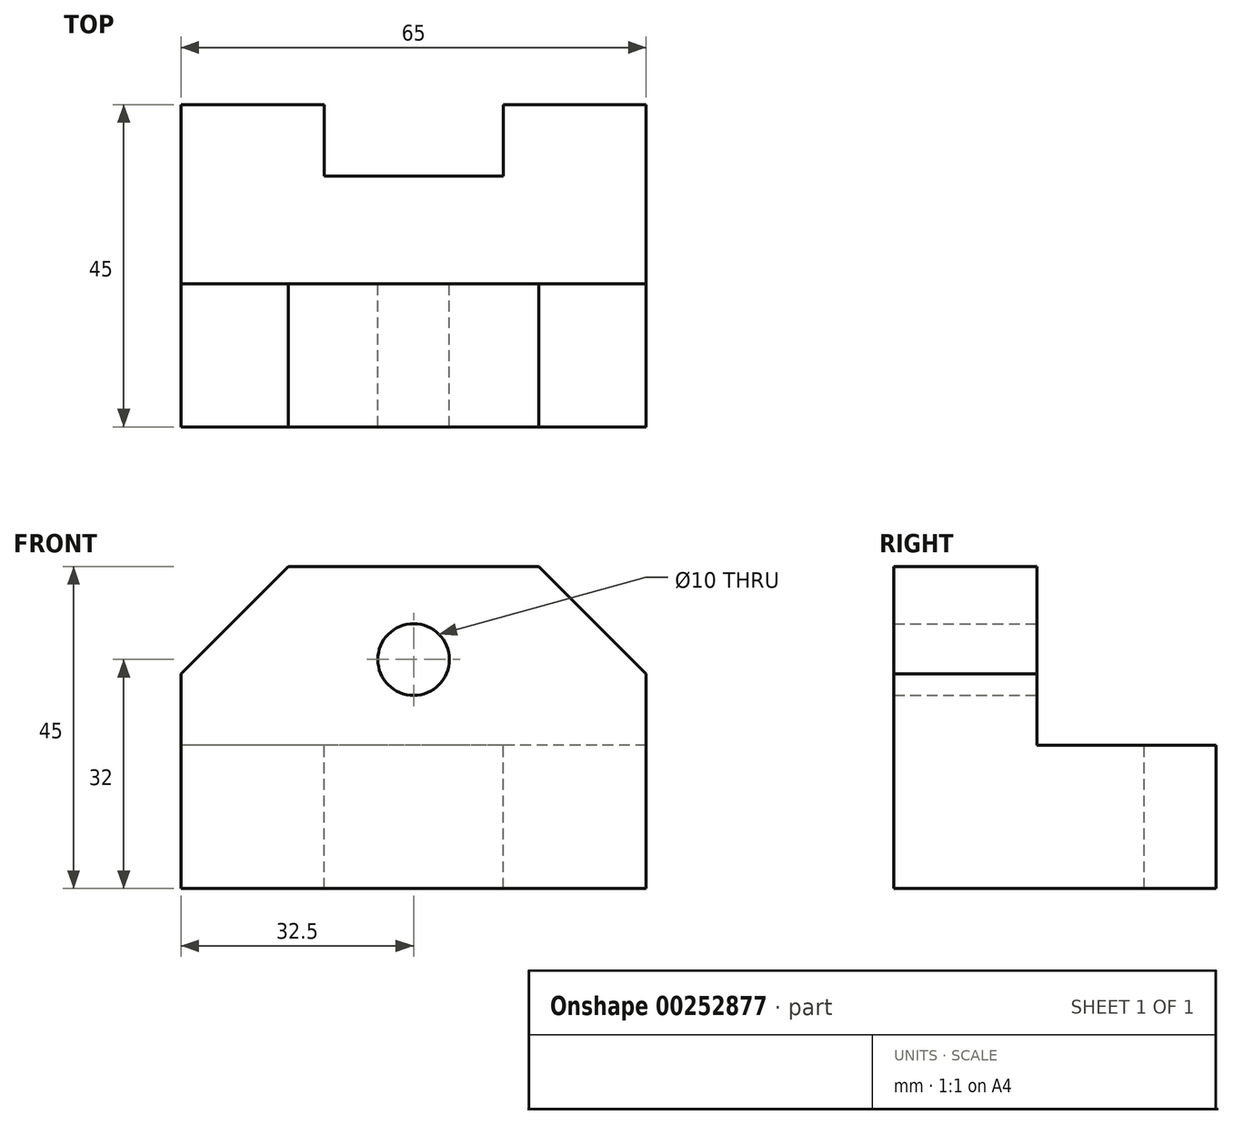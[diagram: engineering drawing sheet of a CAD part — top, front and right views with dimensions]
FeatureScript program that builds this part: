
annotation { "Feature Type Name" : "Feature", "Feature Type Description" : "" }
export const myFeature = defineFeature(function(context is Context, id is Id, definition is map)
    precondition{}
    {
        {
            var Q0;
            Q0=qCreatedBy(makeId("Right.planeOp"),FACE);
            var sketch = newSketch(context, id + "F0", { "sketchPlane" : qUnion([Q0])});
            skLineSegment(sketch, "E0", {"start": v(0, 0) * mm, "end": v(0, 45) * mm});
            skLineSegment(sketch, "E1", {"start": v(0, 45) * mm, "end": v(20, 45) * mm});
            skLineSegment(sketch, "E2", {"start": v(20, 45) * mm, "end": v(20, 20) * mm});
            skLineSegment(sketch, "E3", {"start": v(20, 20) * mm, "end": v(45, 20) * mm});
            skLineSegment(sketch, "E4", {"start": v(45, 20) * mm, "end": v(45, 0) * mm});
            skLineSegment(sketch, "E5", {"start": v(45, 0) * mm, "end": v(0, 0) * mm});
            skSolve(sketch);
        }
        {
            var Q0;
            Q0=makeQuery(id+"F0.imprint","IMPRINT",FACE,{"disambiguationData":[TD([[makeQuery(id+"F0.imprint","IMPRINT",EDGE,{"derivedFrom":sQuery(id+"F0.wireOp",EDGE,"E0")}),-1.0]])]});
            extrude(context, id + "F1", {"entities" : qUnion([Q0]), "depth" : 65 * mm, "symmetric" : true});
        }
        {
            var Q0;
            Q0=makeQuery(id+"F1.opExtrude","SWEPT_FACE",FACE,{"disambiguationData":[OSD([sQuery(id+"F0.wireOp",EDGE,"E3")])]});
            var sketch = newSketch(context, id + "F2", { "sketchPlane" : qUnion([Q0])});
            skLineSegment(sketch, "E6.top", {"start": v(12.5, 35) * mm, "end": v(-12.5, 35) * mm});
            skLineSegment(sketch, "E6.left", {"start": v(12.5, 45) * mm, "end": v(12.5, 35) * mm});
            skLineSegment(sketch, "E6.right", {"start": v(-12.5, 45) * mm, "end": v(-12.5, 35) * mm});
            skPoint(sketch, "E6.middle", {"position": v(0, 45) * mm});
            skLineSegment(sketch, "E7", {"start": v(-12.5, 45) * mm, "end": v(12.5, 45) * mm});
            skPoint(sketch, "E6.bottom.end.orphan", {"position": v(-12.5, 55) * mm});
            skPoint(sketch, "E8.orphan", {"position": v(12.5, 55) * mm});
            skSolve(sketch);
        }
        {
            var Q0;
            Q0=makeQuery(id+"F2.imprint","IMPRINT",FACE,{"disambiguationData":[TD([[makeQuery(id+"F2.imprint","IMPRINT",EDGE,{"derivedFrom":sQuery(id+"F2.wireOp",EDGE,"E6.top")}),-1.0]])]});
            extrude(context, id + "F3", {"entities" : qUnion([Q0]), "operationType" : NewBodyOperationType.REMOVE, "endBound" : BoundingType.THROUGH_ALL, "oppositeDirection" : true, "depth" : 25 * mm});
        }
        {
            var Q0;
            Q0=makeQuery(id+"F1.opExtrude","CAP_EDGE",EDGE,{"disambiguationData":[OSD([sQuery(id+"F0.wireOp",EDGE,"E1")])],"isStart":false});
            var Q1;
            Q1=makeQuery(id+"F1.opExtrude","CAP_EDGE",EDGE,{"disambiguationData":[OSD([sQuery(id+"F0.wireOp",EDGE,"E1")])],"isStart":true});
            chamfer(context, id + "F4", {"entities" : qUnion([Q0, Q1]), "width" : 15 * mm, "tangentPropagation" : true});
        }
        {
            var Q0;
            Q0=makeQuery(id+"F1.opExtrude","SWEPT_FACE",FACE,{"disambiguationData":[OSD([sQuery(id+"F0.wireOp",EDGE,"E2")])]});
            var sketch = newSketch(context, id + "F5", { "sketchPlane" : qUnion([Q0])});
            skCircle(sketch, "E9", {"center": v(0, 32) * mm, "radius": 5 * mm});
            skSolve(sketch);
        }
        {
            var Q0;
            Q0=makeQuery(id+"F5.imprint","IMPRINT",FACE,{"disambiguationData":[TD([[makeQuery(id+"F5.imprint","IMPRINT",EDGE,{"derivedFrom":sQuery(id+"F5.wireOp",EDGE,"E9")}),1.0]])]});
            extrude(context, id + "F6", {"entities" : qUnion([Q0]), "operationType" : NewBodyOperationType.REMOVE, "endBound" : BoundingType.THROUGH_ALL, "oppositeDirection" : true, "depth" : 25 * mm});
        }
    });
